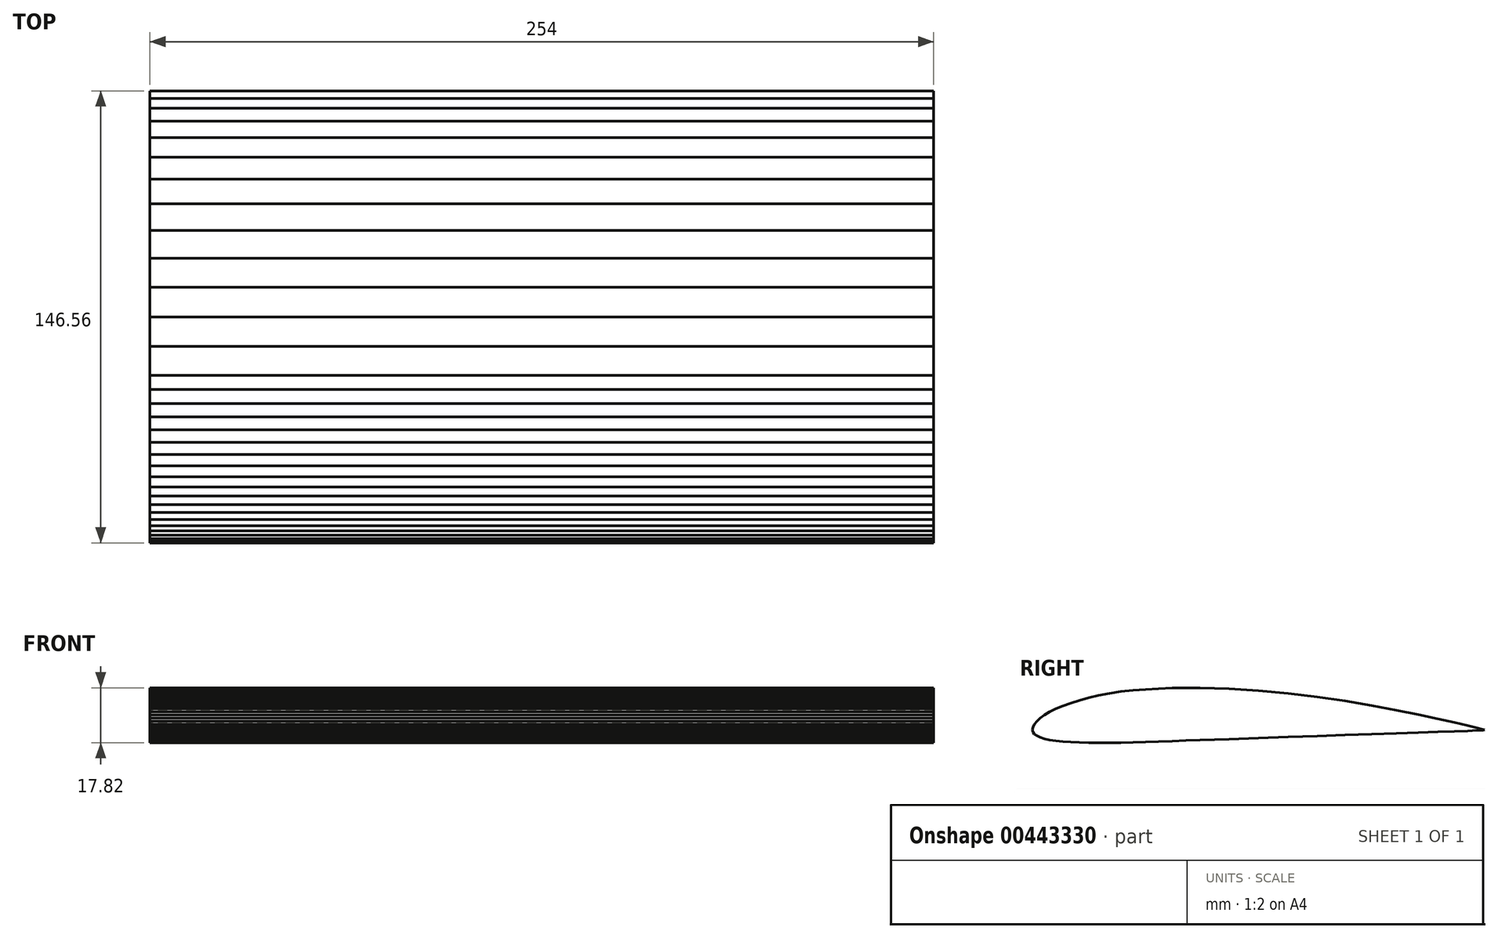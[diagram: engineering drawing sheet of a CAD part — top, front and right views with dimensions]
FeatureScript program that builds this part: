
annotation { "Feature Type Name" : "Feature", "Feature Type Description" : "" }
export const myFeature = defineFeature(function(context is Context, id is Id, definition is map)
    precondition{}
    {
        {
            var Q0;
            Q0=qCreatedBy(makeId("Right.planeOp"),FACE);
            var sketch = newSketch(context, id + "F0", { "sketchPlane" : qUnion([Q0])});
            skLineSegment(sketch, "E0", {"start": v(71.77, -4.58) * mm, "end": v(69.9, -4.1) * mm});
            skLineSegment(sketch, "E1", {"start": v(72.4, -4.75) * mm, "end": v(71.77, -4.58) * mm});
            skLineSegment(sketch, "E2", {"start": v(69.9, -4.1) * mm, "end": v(66.82, -3.32) * mm});
            skLineSegment(sketch, "E3", {"start": v(66.82, -3.32) * mm, "end": v(62.58, -2.32) * mm});
            skLineSegment(sketch, "E4", {"start": v(62.58, -2.32) * mm, "end": v(57.26, -1.12) * mm});
            skLineSegment(sketch, "E5", {"start": v(57.26, -1.12) * mm, "end": v(50.94, 0.24) * mm});
            skLineSegment(sketch, "E6", {"start": v(50.94, 0.24) * mm, "end": v(43.73, 1.7) * mm});
            skLineSegment(sketch, "E7", {"start": v(43.73, 1.7) * mm, "end": v(35.76, 3.18) * mm});
            skLineSegment(sketch, "E8", {"start": v(35.76, 3.18) * mm, "end": v(27.16, 4.64) * mm});
            skLineSegment(sketch, "E9", {"start": v(27.16, 4.64) * mm, "end": v(18.09, 5.98) * mm});
            skLineSegment(sketch, "E10", {"start": v(18.09, 5.98) * mm, "end": v(8.69, 7.13) * mm});
            skLineSegment(sketch, "E11", {"start": v(8.69, 7.13) * mm, "end": v(-0.88, 8.03) * mm});
            skLineSegment(sketch, "E12", {"start": v(-0.88, 8.03) * mm, "end": v(-10.44, 8.63) * mm});
            skLineSegment(sketch, "E13", {"start": v(-10.44, 8.63) * mm, "end": v(-19.85, 8.9) * mm});
            skLineSegment(sketch, "E14", {"start": v(-19.85, 8.9) * mm, "end": v(-24.43, 8.9) * mm});
            skLineSegment(sketch, "E15", {"start": v(-24.43, 8.9) * mm, "end": v(-28.92, 8.83) * mm});
            skLineSegment(sketch, "E16", {"start": v(-28.92, 8.83) * mm, "end": v(-33.29, 8.67) * mm});
            skLineSegment(sketch, "E17", {"start": v(-33.29, 8.67) * mm, "end": v(-37.52, 8.44) * mm});
            skLineSegment(sketch, "E18", {"start": v(-37.52, 8.44) * mm, "end": v(-41.6, 8.11) * mm});
            skLineSegment(sketch, "E19", {"start": v(-41.6, 8.11) * mm, "end": v(-45.49, 7.68) * mm});
            skLineSegment(sketch, "E20", {"start": v(-49.2, 7.14) * mm, "end": v(-52.7, 6.48) * mm});
            skLineSegment(sketch, "E21", {"start": v(-19.85, -8.03) * mm, "end": v(-10.44, -7.7) * mm});
            skLineSegment(sketch, "E22", {"start": v(-24.43, -8.2) * mm, "end": v(-19.85, -8.03) * mm});
            skLineSegment(sketch, "E23", {"start": v(-28.92, -8.35) * mm, "end": v(-24.43, -8.2) * mm});
            skLineSegment(sketch, "E24", {"start": v(-33.29, -8.5) * mm, "end": v(-28.92, -8.35) * mm});
            skLineSegment(sketch, "E25", {"start": v(-37.52, -8.64) * mm, "end": v(-33.29, -8.5) * mm});
            skLineSegment(sketch, "E26", {"start": v(-41.6, -8.75) * mm, "end": v(-37.52, -8.64) * mm});
            skLineSegment(sketch, "E27", {"start": v(-45.49, -8.84) * mm, "end": v(-41.6, -8.75) * mm});
            skLineSegment(sketch, "E28", {"start": v(-49.2, -8.9) * mm, "end": v(-45.49, -8.84) * mm});
            skLineSegment(sketch, "E29", {"start": v(-52.7, -8.9) * mm, "end": v(-49.2, -8.9) * mm});
            skLineSegment(sketch, "E30", {"start": v(-55.97, -8.87) * mm, "end": v(-52.7, -8.9) * mm});
            skLineSegment(sketch, "E31", {"start": v(-59.02, -8.8) * mm, "end": v(-55.97, -8.87) * mm});
            skLineSegment(sketch, "E32", {"start": v(-61.8, -8.68) * mm, "end": v(-59.02, -8.8) * mm});
            skLineSegment(sketch, "E33", {"start": v(-64.34, -8.5) * mm, "end": v(-61.8, -8.68) * mm});
            skLineSegment(sketch, "E34", {"start": v(-70.27, -7.62) * mm, "end": v(-68.58, -8) * mm});
            skLineSegment(sketch, "E35", {"start": v(-71.66, -7.17) * mm, "end": v(-70.27, -7.62) * mm});
            skLineSegment(sketch, "E36", {"start": v(-72.75, -6.65) * mm, "end": v(-71.66, -7.17) * mm});
            skLineSegment(sketch, "E37", {"start": v(-73.53, -6.06) * mm, "end": v(-72.75, -6.65) * mm});
            skLineSegment(sketch, "E38", {"start": v(-74, -5.41) * mm, "end": v(-73.53, -6.06) * mm});
            skLineSegment(sketch, "E39", {"start": v(-74.16, -4.68) * mm, "end": v(-74, -5.41) * mm});
            skLineSegment(sketch, "E40", {"start": v(-74, -3.84) * mm, "end": v(-74.16, -4.68) * mm});
            skLineSegment(sketch, "E41", {"start": v(-73.53, -2.9) * mm, "end": v(-74, -3.84) * mm});
            skLineSegment(sketch, "E42", {"start": v(-72.75, -1.9) * mm, "end": v(-73.53, -2.9) * mm});
            skLineSegment(sketch, "E43", {"start": v(-71.66, -0.86) * mm, "end": v(-72.75, -1.9) * mm});
            skLineSegment(sketch, "E44", {"start": v(-70.27, 0.16) * mm, "end": v(-71.66, -0.86) * mm});
            skLineSegment(sketch, "E45", {"start": v(-68.58, 1.15) * mm, "end": v(-70.27, 0.16) * mm});
            skLineSegment(sketch, "E46", {"start": v(-66.6, 2.1) * mm, "end": v(-68.58, 1.15) * mm});
            skLineSegment(sketch, "E47", {"start": v(-64.34, 3.04) * mm, "end": v(-66.6, 2.1) * mm});
            skLineSegment(sketch, "E48", {"start": v(-61.8, 3.96) * mm, "end": v(-64.34, 3.04) * mm});
            skLineSegment(sketch, "E49", {"start": v(-59.02, 4.85) * mm, "end": v(-61.8, 3.96) * mm});
            skLineSegment(sketch, "E50", {"start": v(-55.97, 5.7) * mm, "end": v(-59.02, 4.85) * mm});
            skLineSegment(sketch, "E51", {"start": v(-68.58, -8) * mm, "end": v(-66.6, -8.29) * mm});
            skLineSegment(sketch, "E52", {"start": v(-45.49, 7.68) * mm, "end": v(-49.2, 7.14) * mm});
            skLineSegment(sketch, "E53", {"start": v(-66.6, -8.29) * mm, "end": v(-64.34, -8.5) * mm});
            skLineSegment(sketch, "E54", {"start": v(-52.7, 6.48) * mm, "end": v(-55.97, 5.7) * mm});
            skLineSegment(sketch, "E55", {"start": v(-10.44, -7.7) * mm, "end": v(-0.88, -7.37) * mm});
            skLineSegment(sketch, "E56", {"start": v(-0.88, -7.37) * mm, "end": v(8.69, -7.04) * mm});
            skLineSegment(sketch, "E57", {"start": v(8.69, -7.04) * mm, "end": v(18.09, -6.72) * mm});
            skLineSegment(sketch, "E58", {"start": v(18.09, -6.72) * mm, "end": v(27.16, -6.4) * mm});
            skLineSegment(sketch, "E59", {"start": v(27.16, -6.4) * mm, "end": v(35.76, -6.1) * mm});
            skLineSegment(sketch, "E60", {"start": v(35.76, -6.1) * mm, "end": v(43.73, -5.83) * mm});
            skLineSegment(sketch, "E61", {"start": v(43.73, -5.83) * mm, "end": v(50.94, -5.6) * mm});
            skLineSegment(sketch, "E62", {"start": v(50.94, -5.6) * mm, "end": v(57.26, -5.38) * mm});
            skLineSegment(sketch, "E63", {"start": v(57.26, -5.38) * mm, "end": v(62.58, -5.2) * mm});
            skLineSegment(sketch, "E64", {"start": v(62.58, -5.2) * mm, "end": v(66.82, -5.03) * mm});
            skLineSegment(sketch, "E65", {"start": v(66.82, -5.03) * mm, "end": v(69.9, -4.89) * mm});
            skLineSegment(sketch, "E66", {"start": v(69.9, -4.89) * mm, "end": v(71.77, -4.78) * mm});
            skLineSegment(sketch, "E67", {"start": v(71.77, -4.78) * mm, "end": v(72.4, -4.75) * mm});
            skLineSegment(sketch, "E68", {"start": v(-74.16, -4.68) * mm, "end": v(-86.47, -4.68) * mm});
            skLineSegment(sketch, "E69", {"start": v(72.4, -4.75) * mm, "end": v(86.47, -4.75) * mm});
            skSolve(sketch);
        }
        {
            var Q0;
            Q0 = qSketchRegion(id + "F0", true);
            extrude(context, id + "F1", {"entities" : qUnion([Q0]), "depth" : 254 * mm});
        }
    });
